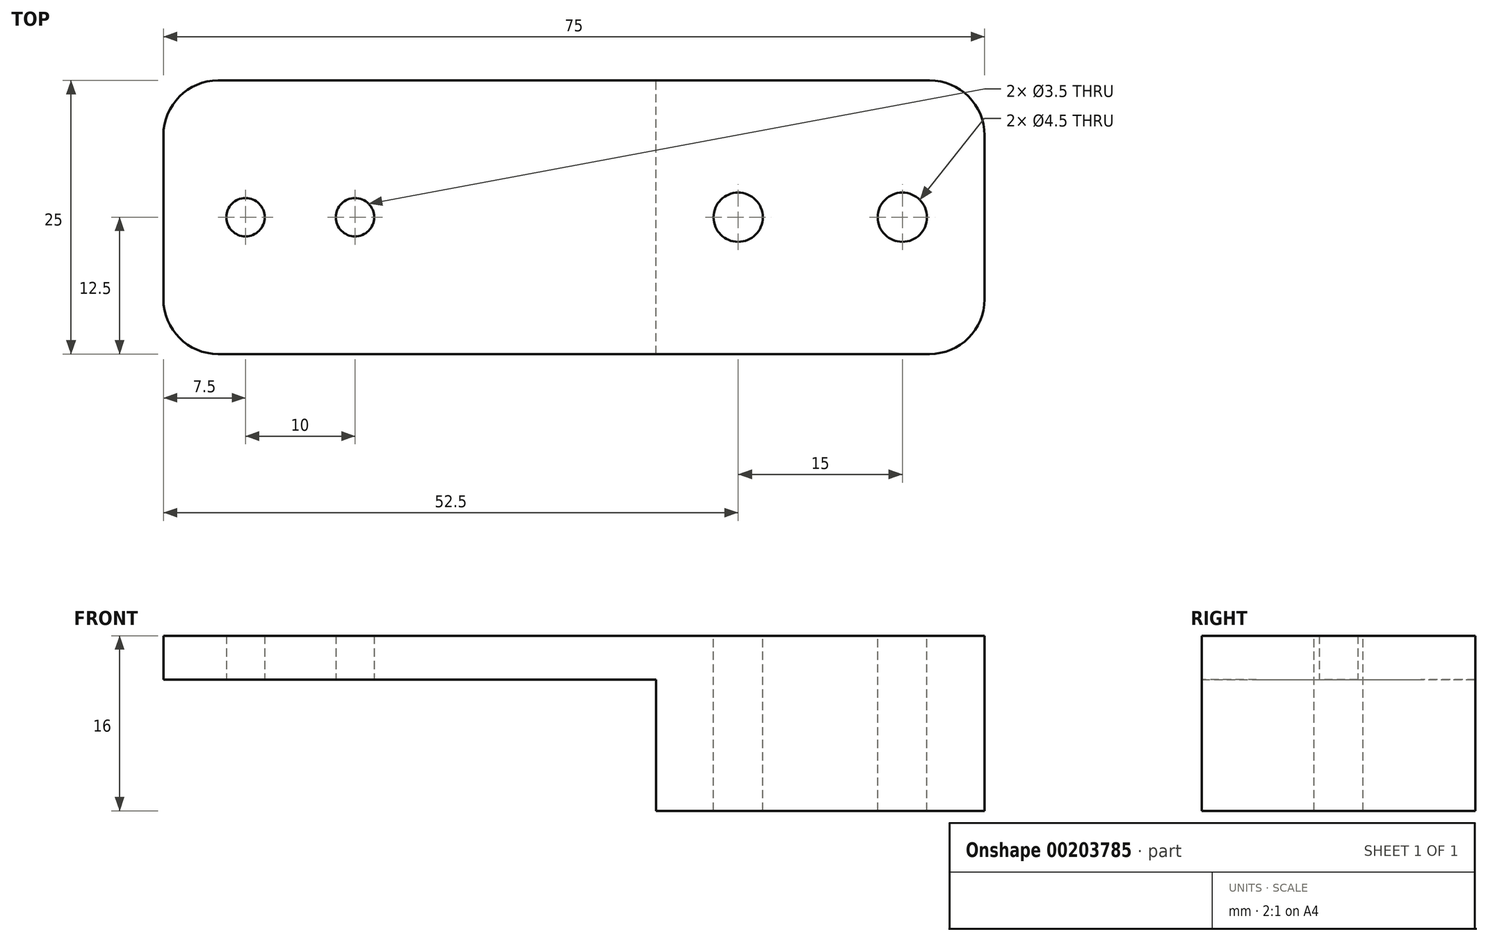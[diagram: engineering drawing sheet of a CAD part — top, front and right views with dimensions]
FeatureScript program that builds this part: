
annotation { "Feature Type Name" : "Feature", "Feature Type Description" : "" }
export const myFeature = defineFeature(function(context is Context, id is Id, definition is map)
    precondition{}
    {
        {
            var Q0;
            Q0=qCreatedBy(makeId("Top.planeOp"),FACE);
            var sketch = newSketch(context, id + "F0", { "sketchPlane" : qUnion([Q0])});
            skLineSegment(sketch, "E0.bottom", {"start": v(37.5, -12.5) * mm, "end": v(-37.5, -12.5) * mm});
            skLineSegment(sketch, "E0.top", {"start": v(37.5, 12.5) * mm, "end": v(-37.5, 12.5) * mm});
            skLineSegment(sketch, "E0.left", {"start": v(37.5, -12.5) * mm, "end": v(37.5, 12.5) * mm});
            skLineSegment(sketch, "E0.right", {"start": v(-37.5, -12.5) * mm, "end": v(-37.5, 12.5) * mm});
            skPoint(sketch, "E0.middle", {"position": v(0, 0) * mm});
            skLineSegment(sketch, "E1", {"start": v(-37.5, 0) * mm, "end": v(-30, 0) * mm, "construction": true});
            skPoint(sketch, "E1.endSnap0", {"position": v(-37.5, 0) * mm});
            skLineSegment(sketch, "E2", {"start": v(-30, 0) * mm, "end": v(-20, 0) * mm, "construction": true});
            skCircle(sketch, "E3", {"center": v(-30, 0) * mm, "radius": 1.75 * mm});
            skCircle(sketch, "E4", {"center": v(-20, 0) * mm, "radius": 1.75 * mm});
            skSolve(sketch);
        }
        {
            var Q0;
            Q0=makeQuery(id+"F0.imprint","IMPRINT",FACE,{"disambiguationData":[TD([[makeQuery(id+"F0.imprint","IMPRINT",EDGE,{"derivedFrom":sQuery(id+"F0.wireOp",EDGE,"E0.bottom")}),-1.0]])]});
            extrude(context, id + "F1", {"entities" : qUnion([Q0]), "depth" : 4 * mm, "symmetric" : true});
        }
        {
            var Q0;
            Q0=makeQuery(id+"F1.opExtrude","CAP_FACE",FACE,{"disambiguationData":[OSD([sQuery(id+"F0.wireOp",EDGE,"E0.bottom"),sQuery(id+"F0.wireOp",EDGE,"E0.top"),sQuery(id+"F0.wireOp",EDGE,"E0.left"),sQuery(id+"F0.wireOp",EDGE,"E0.right"),sQuery(id+"F0.wireOp",EDGE,"E3"),sQuery(id+"F0.wireOp",EDGE,"E4")])],"isStart":true});
            var sketch = newSketch(context, id + "F2", { "sketchPlane" : qUnion([Q0])});
            skLineSegment(sketch, "E5", {"start": v(37.5, 12.5) * mm, "end": v(7.5, 12.5) * mm});
            skLineSegment(sketch, "E6", {"start": v(7.5, 12.5) * mm, "end": v(7.5, -12.5) * mm});
            skLineSegment(sketch, "E7", {"start": v(7.5, -12.5) * mm, "end": v(37.5, -12.5) * mm});
            skLineSegment(sketch, "E8", {"start": v(37.5, -12.5) * mm, "end": v(37.5, 12.5) * mm});
            skLineSegment(sketch, "E9", {"start": v(37.5, 0) * mm, "end": v(30, 0) * mm, "construction": true});
            skPoint(sketch, "E9.endSnap0", {"position": v(37.5, 0) * mm});
            skLineSegment(sketch, "E10", {"start": v(30, 0) * mm, "end": v(15, 0) * mm, "construction": true});
            skCircle(sketch, "E11", {"center": v(15, 0) * mm, "radius": 2.25 * mm});
            skCircle(sketch, "E12", {"center": v(30, 0) * mm, "radius": 2.25 * mm});
            skSolve(sketch);
        }
        {
            var Q0;
            Q0=makeQuery(id+"F2.imprint","IMPRINT",FACE,{"disambiguationData":[TD([[makeQuery(id+"F2.imprint","IMPRINT",EDGE,{"derivedFrom":sQuery(id+"F2.wireOp",EDGE,"E5")}),1.0]])]});
            extrude(context, id + "F3", {"entities" : qUnion([Q0]), "operationType" : NewBodyOperationType.ADD, "depth" : 12 * mm});
        }
        {
            var Q0;
            Q0=makeQuery(id+"F3.boolean.opBoolean","SPLIT",FACE,{"disambiguationData":[TD([makeQuery(id+"F3.opExtrude","SWEPT_FACE",FACE,{"disambiguationData":[OSD([sQuery(id+"F2.wireOp",EDGE,"E11")])]})])],"derivedFrom":makeQuery(id+"F1.opExtrude","CAP_FACE",FACE,{"disambiguationData":[OSD([sQuery(id+"F0.wireOp",EDGE,"E0.bottom"),sQuery(id+"F0.wireOp",EDGE,"E0.top"),sQuery(id+"F0.wireOp",EDGE,"E0.left"),sQuery(id+"F0.wireOp",EDGE,"E0.right"),sQuery(id+"F0.wireOp",EDGE,"E3"),sQuery(id+"F0.wireOp",EDGE,"E4")])],"isStart":true})});
            var Q1;
            Q1=makeQuery(id+"F3.boolean.opBoolean","SPLIT",FACE,{"disambiguationData":[TD([makeQuery(id+"F3.opExtrude","SWEPT_FACE",FACE,{"disambiguationData":[OSD([sQuery(id+"F2.wireOp",EDGE,"E12")])]})])],"derivedFrom":makeQuery(id+"F1.opExtrude","CAP_FACE",FACE,{"disambiguationData":[OSD([sQuery(id+"F0.wireOp",EDGE,"E0.bottom"),sQuery(id+"F0.wireOp",EDGE,"E0.top"),sQuery(id+"F0.wireOp",EDGE,"E0.left"),sQuery(id+"F0.wireOp",EDGE,"E0.right"),sQuery(id+"F0.wireOp",EDGE,"E3"),sQuery(id+"F0.wireOp",EDGE,"E4")])],"isStart":true})});
            extrude(context, id + "F4", {"entities" : qUnion([Q0, Q1]), "operationType" : NewBodyOperationType.REMOVE, "endBound" : BoundingType.UP_TO_NEXT, "oppositeDirection" : true, "depth" : 25 * mm});
        }
        {
            var Q0;
            Q0=makeQuery(id+"F1.opExtrude","SWEPT_EDGE",EDGE,{"disambiguationData":[OSD([sQuery(id+"F0.wireOp",EDGE,"E0.top"),sQuery(id+"F0.wireOp",EDGE,"E0.right")])]});
            var Q1;
            Q1=makeQuery(id+"F1.opExtrude","SWEPT_EDGE",EDGE,{"disambiguationData":[OSD([sQuery(id+"F0.wireOp",EDGE,"E0.bottom"),sQuery(id+"F0.wireOp",EDGE,"E0.right")])]});
            var Q2;
            Q2=makeQuery(id+"F3.opExtrude","CAP_EDGE",EDGE,{"disambiguationData":[OSD([sQuery(id+"F2.wireOp",EDGE,"E6")])],"isStart":true});
            var Q3;
            Q3=makeQuery(id+"F3.boolean.opBoolean","MERGE",EDGE,{"derivedFrom":[makeQuery(id+"F1.opExtrude","SWEPT_EDGE",EDGE,{"disambiguationData":[OSD([sQuery(id+"F0.wireOp",EDGE,"E0.bottom"),sQuery(id+"F0.wireOp",EDGE,"E0.left")])]}),makeQuery(id+"F3.opExtrude","SWEPT_EDGE",EDGE,{"disambiguationData":[OSD([sQuery(id+"F2.wireOp",EDGE,"E5"),sQuery(id+"F2.wireOp",EDGE,"E8")])]})]});
            var Q4;
            Q4=makeQuery(id+"F3.boolean.opBoolean","MERGE",EDGE,{"derivedFrom":[makeQuery(id+"F1.opExtrude","SWEPT_EDGE",EDGE,{"disambiguationData":[OSD([sQuery(id+"F0.wireOp",EDGE,"E0.top"),sQuery(id+"F0.wireOp",EDGE,"E0.left")])]}),makeQuery(id+"F3.opExtrude","SWEPT_EDGE",EDGE,{"disambiguationData":[OSD([sQuery(id+"F2.wireOp",EDGE,"E7"),sQuery(id+"F2.wireOp",EDGE,"E8")])]})]});
            fillet(context, id + "F5", {"entities" : qUnion([Q0, Q1, Q2, Q3, Q4]), "radius" : 5 * mm, "tangentPropagation" : true, "allowEdgeOverflow" : false});
        }
    });
